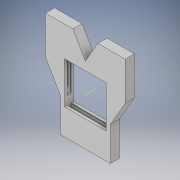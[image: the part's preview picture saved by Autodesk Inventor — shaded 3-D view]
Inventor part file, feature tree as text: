
AUTODESK INVENTOR PART (.ipt)
format: ipt  version: 2017 (Build 210142000, 142)  size: 304,128 bytes
history: native  units: in
note: dims shown in document units (in); Inventor stores cm internally (conversion verified against a paired STEP export)
features: extrude x7, sketch x7, other x3
ambient origin geometry x8: Origin, YZ Plane, XZ Plane, XY Plane, X Axis, Y Axis, Z Axis, Center Point
bodies: Body1 (feature_tree)
feature tree (17):
  other  "rame of door"
  extrude  "frame"  Depth=100.0in
  other  "middle of part"
  extrude  "door slot bottom"  Depth=10.0in
  extrude  "top left and right slots"  Depth=10.0in
  extrude  "slots for hiding bars"  Depth=22.0in
  extrude  "door recieves"  Depth=10.0in TaperAngle=0.0deg
  extrude  "front hide door"  Depth=2.0in
  extrude  "gap for door pieces"  Depth=1.0in
  other  "mate for door pieces"
  sketch  "Sketch1"  dims[d0=100.0in d1=100.0in]
  sketch  "Sketch7"  dims[d3=10.0in d4=10.0in]
  sketch  "Sketch8"  dims[d5=10.0in d6=10.0in]
  sketch  "Sketch12"  dims[d7=22.0in d8=0.0in d118=0.7071in d178=0.8316in]
  sketch  "Sketch13"  dims[d459=10.0in d460=0.0in d865=10.0in d866=0.0in]
  sketch  "Sketch14"  dims[d878=60.0deg d889=2.0in]
  sketch  "Sketch15"  dims[d890=1.0in d891=1.0in d893=1.0in d894=1.0in d895=1.0in d898=20.0in d899=0.0in d901=2.0in d902=78.8675in d903=51.0in d907=10.0in d916=10.0in d917=10.0in d919=10.0in d920=10.0in d921=10.0in d922=22.0in d923=0.0in d926=25.7957in d927=52.0in d928=21.0in d929=0.0in d930=10.0in d931=0.0in d932=50.0in]
